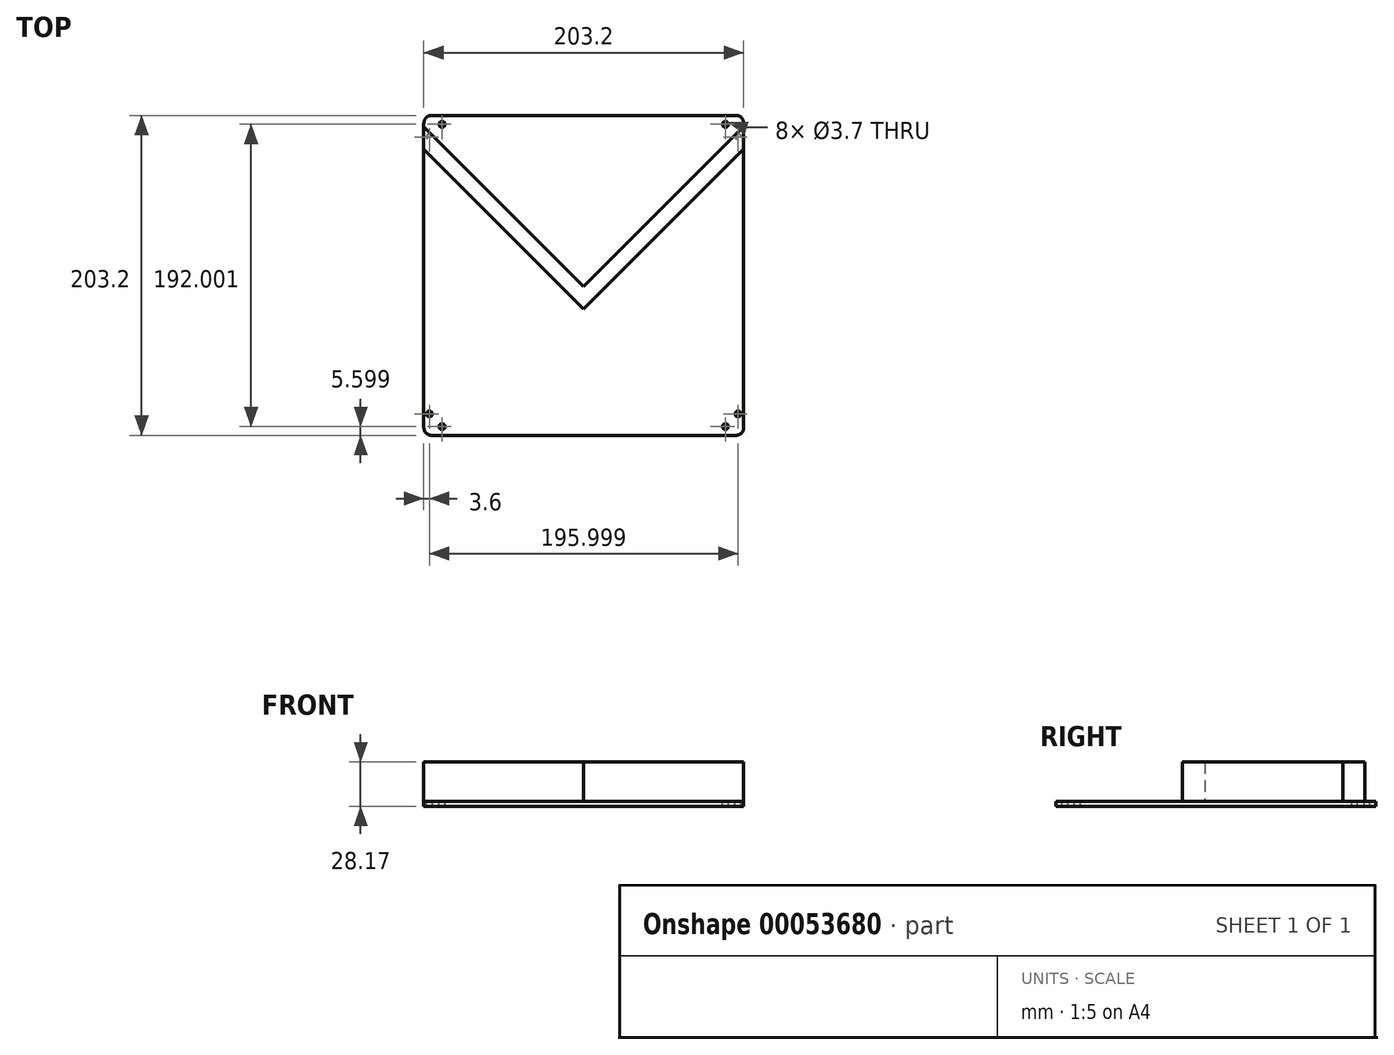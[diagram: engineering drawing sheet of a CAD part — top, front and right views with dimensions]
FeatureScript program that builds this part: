
annotation { "Feature Type Name" : "Feature", "Feature Type Description" : "" }
export const myFeature = defineFeature(function(context is Context, id is Id, definition is map)
    precondition{}
    {
        {
            var Q0;
            Q0=qCreatedBy(makeId("Top.planeOp"),FACE);
            var sketch = newSketch(context, id + "F0", { "sketchPlane" : qUnion([Q0])});
            skLineSegment(sketch, "E0.rect.bottom", {"start": v(101.6, 101.6) * mm, "end": v(-101.6, 101.6) * mm});
            skLineSegment(sketch, "E0.rect.top", {"start": v(101.6, -101.6) * mm, "end": v(-101.6, -101.6) * mm});
            skLineSegment(sketch, "E0.rect.left", {"start": v(101.6, 101.6) * mm, "end": v(101.6, -101.6) * mm});
            skLineSegment(sketch, "E0.rect.right", {"start": v(-101.6, 101.6) * mm, "end": v(-101.6, -101.6) * mm});
            skPoint(sketch, "E0.rect.middle", {"position": v(0, 0) * mm});
            skSolve(sketch);
        }
        {
            var Q0;
            Q0=makeQuery(id+"F0.imprint","IMPRINT",FACE,{"disambiguationData":[TD([[makeQuery(id+"F0.imprint","IMPRINT",EDGE,{"derivedFrom":sQuery(id+"F0.wireOp",EDGE,"E0.rect.bottom")}),1.0]])]});
            extrude(context, id + "F1", {"entities" : qUnion([Q0]), "depth" : 3.17 * mm});
        }
        {
            var Q0;
            Q0=makeQuery(id+"F1.opExtrude","CAP_FACE",FACE,{"disambiguationData":[OSD([sQuery(id+"F0.wireOp",EDGE,"E0.rect.bottom"),sQuery(id+"F0.wireOp",EDGE,"E0.rect.top"),sQuery(id+"F0.wireOp",EDGE,"E0.rect.left"),sQuery(id+"F0.wireOp",EDGE,"E0.rect.right")])],"isStart":false});
            var sketch = newSketch(context, id + "F2", { "sketchPlane" : qUnion([Q0])});
            skLineSegment(sketch, "E1", {"start": v(0, 0) * mm, "end": v(98, 0) * mm});
            skLineSegment(sketch, "E2", {"start": v(0, 0) * mm, "end": v(-98, 0) * mm});
            skLineSegment(sketch, "E3", {"start": v(98, 0) * mm, "end": v(98, 92) * mm});
            skLineSegment(sketch, "E4", {"start": v(-98, 0) * mm, "end": v(-98, 92) * mm});
            skLineSegment(sketch, "E5", {"start": v(-98, 0) * mm, "end": v(-98, -92) * mm});
            skLineSegment(sketch, "E6", {"start": v(98, 0) * mm, "end": v(98, -92) * mm});
            skArc(sketch, "E7", {"start": v(-99.85, 99.54) * mm, "mid": v(-97.04, 92.12) * mm, "end": v(-98, 100) * mm});
            skPoint(sketch, "E7.centerSnap0", {"position": v(-94, 96) * mm});
            skPoint(sketch, "E7.centerSnap1", {"position": v(-98, 100) * mm});
            skPoint(sketch, "E8", {"position": v(-98, 92) * mm});
            skArc(sketch, "E9", {"start": v(96.25, 99.6) * mm, "mid": v(98.9, 92.1) * mm, "end": v(98, 100) * mm});
            skPoint(sketch, "E9.centerSnap0", {"position": v(102, 96) * mm});
            skPoint(sketch, "E9.centerSnap1", {"position": v(98, 100) * mm});
            skPoint(sketch, "E10", {"position": v(98, 92) * mm});
            skPoint(sketch, "E11", {"position": v(98, -100) * mm});
            skPoint(sketch, "E12.centerSnap0", {"position": v(102, -96) * mm});
            skPoint(sketch, "E12.centerSnap1", {"position": v(98, -92) * mm});
            skArc(sketch, "E12", {"start": v(101.9, -95.08) * mm, "mid": v(94.03, -96.47) * mm, "end": v(102, -96) * mm});
            skPoint(sketch, "E13", {"position": v(-98, -100) * mm});
            skPoint(sketch, "E14.centerSnap0", {"position": v(-94, -96) * mm});
            skPoint(sketch, "E14.centerSnap1", {"position": v(-98, -92) * mm});
            skArc(sketch, "E14", {"start": v(-101.6, -94.26) * mm, "mid": v(-95.01, -98.66) * mm, "end": v(-100.15, -92.63) * mm});
            skPoint(sketch, "E15.right.end.orphan", {"position": v(-102, -92) * mm});
            skPoint(sketch, "E16.orphan", {"position": v(-94, -92) * mm});
            skPoint(sketch, "E17.orphan", {"position": v(-94, -100) * mm});
            skPoint(sketch, "E15.bottom.end.orphan", {"position": v(-102, -100) * mm});
            skPoint(sketch, "E18.orphan", {"position": v(-94, 100) * mm});
            skPoint(sketch, "E19.orphan", {"position": v(-94, 92) * mm});
            skPoint(sketch, "E20.orphan", {"position": v(-102, 92) * mm});
            skPoint(sketch, "E21.top.end.orphan", {"position": v(-102, 100) * mm});
            skPoint(sketch, "E22.orphan", {"position": v(102, 100) * mm});
            skPoint(sketch, "E23.orphan", {"position": v(102, 92) * mm});
            skPoint(sketch, "E24.orphan", {"position": v(94, 92) * mm});
            skPoint(sketch, "E25.right.end.orphan", {"position": v(94, 100) * mm});
            skPoint(sketch, "E26.orphan", {"position": v(102, -92) * mm});
            skPoint(sketch, "E27.orphan", {"position": v(94, -100) * mm});
            skPoint(sketch, "E28.right.end.orphan", {"position": v(94, -92) * mm});
            skPoint(sketch, "E28.bottom.start.orphan", {"position": v(102, -100) * mm});
            skCircle(sketch, "E29", {"center": v(-90, 96) * mm, "radius": 1.85 * mm});
            skCircle(sketch, "E30", {"center": v(-98, 88) * mm, "radius": 1.85 * mm});
            skCircle(sketch, "E31", {"center": v(98, 88) * mm, "radius": 1.85 * mm});
            skCircle(sketch, "E32", {"center": v(90, 96) * mm, "radius": 1.85 * mm});
            skCircle(sketch, "E33", {"center": v(98, -88) * mm, "radius": 1.85 * mm});
            skCircle(sketch, "E34", {"center": v(90, -96) * mm, "radius": 1.85 * mm});
            skCircle(sketch, "E35", {"center": v(-90, -96) * mm, "radius": 1.85 * mm});
            skCircle(sketch, "E36", {"center": v(-98, -88) * mm, "radius": 1.85 * mm});
            skPoint(sketch, "E37", {"position": v(-100.15, -92.63) * mm});
            skPoint(sketch, "E38", {"position": v(-101.6, -94.26) * mm});
            skPoint(sketch, "E39", {"position": v(-99.85, 99.54) * mm});
            skPoint(sketch, "E40", {"position": v(96.25, 99.6) * mm});
            skPoint(sketch, "E41", {"position": v(101.9, -95.08) * mm});
            skSolve(sketch);
        }
        {
            var Q0;
            Q0 = qSketchRegion(id + "F2", true);
            extrude(context, id + "F3", {"entities" : qUnion([Q0]), "operationType" : NewBodyOperationType.REMOVE, "oppositeDirection" : true, "depth" : 25.4 * mm});
        }
        {
            var Q0;
            Q0=makeQuery(id+"F1.opExtrude","SWEPT_EDGE",EDGE,{"disambiguationData":[OSD([sQuery(id+"F0.wireOp",EDGE,"E0.rect.bottom"),sQuery(id+"F0.wireOp",EDGE,"E0.rect.right")])]});
            fillet(context, id + "F4", {"entities" : qUnion([Q0]), "radius" : 5.08 * mm, "tangentPropagation" : true, "allowEdgeOverflow" : false});
        }
        {
            var Q0;
            Q0=makeQuery(id+"F1.opExtrude","SWEPT_EDGE",EDGE,{"disambiguationData":[OSD([sQuery(id+"F0.wireOp",EDGE,"E0.rect.bottom"),sQuery(id+"F0.wireOp",EDGE,"E0.rect.left")])]});
            var Q1;
            Q1=makeQuery(id+"F1.opExtrude","SWEPT_EDGE",EDGE,{"disambiguationData":[OSD([sQuery(id+"F0.wireOp",EDGE,"E0.rect.top"),sQuery(id+"F0.wireOp",EDGE,"E0.rect.left")])]});
            var Q2;
            Q2=makeQuery(id+"F1.opExtrude","SWEPT_EDGE",EDGE,{"disambiguationData":[OSD([sQuery(id+"F0.wireOp",EDGE,"E0.rect.top"),sQuery(id+"F0.wireOp",EDGE,"E0.rect.right")])]});
            fillet(context, id + "F5", {"entities" : qUnion([Q0, Q1, Q2]), "radius" : 5.08 * mm, "tangentPropagation" : true, "allowEdgeOverflow" : false});
        }
        {
            var Q0;
            Q0=makeQuery(id+"F1.opExtrude","CAP_FACE",FACE,{"disambiguationData":[OSD([sQuery(id+"F0.wireOp",EDGE,"E0.rect.bottom"),sQuery(id+"F0.wireOp",EDGE,"E0.rect.top"),sQuery(id+"F0.wireOp",EDGE,"E0.rect.left"),sQuery(id+"F0.wireOp",EDGE,"E0.rect.right")])],"isStart":false});
            var sketch = newSketch(context, id + "F6", { "sketchPlane" : qUnion([Q0])});
            skPoint(sketch, "E42", {"position": v(2.96, -10.03) * mm});
            skPoint(sketch, "E43", {"position": v(-101.6, 94.53) * mm});
            skPoint(sketch, "E44", {"position": v(101.6, 94.53) * mm});
            skPoint(sketch, "E45", {"position": v(52.93, 31.72) * mm});
            skLineSegment(sketch, "E46", {"start": v(-101.6, 94.53) * mm, "end": v(0, -7.07) * mm});
            skLineSegment(sketch, "E47", {"start": v(0, -7.07) * mm, "end": v(101.6, 94.53) * mm});
            skLineSegment(sketch, "E48", {"start": v(52.93, 31.72) * mm, "end": v(101.6, 80.39) * mm});
            skLineSegment(sketch, "E49", {"start": v(52.93, 31.72) * mm, "end": v(7.07, -14.14) * mm});
            skLineSegment(sketch, "E50", {"start": v(0, -7.07) * mm, "end": v(0, -3.45) * mm});
            skLineSegment(sketch, "E51", {"start": v(-101.6, 80.39) * mm, "end": v(-101.6, 94.53) * mm});
            skPoint(sketch, "E52", {"position": v(0, -21.21) * mm});
            skLineSegment(sketch, "E53", {"start": v(0, -21.21) * mm, "end": v(-101.6, 80.39) * mm});
            skLineSegment(sketch, "E54", {"start": v(101.6, 94.53) * mm, "end": v(101.6, 80.39) * mm});
            skPoint(sketch, "E55", {"position": v(3.89, -10.96) * mm});
            skLineSegment(sketch, "E56", {"start": v(0, -21.21) * mm, "end": v(7.07, -14.14) * mm});
            skLineSegment(sketch, "E57", {"start": v(0, -7.07) * mm, "end": v(2.96, -10.03) * mm});
            skLineSegment(sketch, "E58.trimOffspring", {"start": v(3.89, -10.96) * mm, "end": v(7.07, -14.14) * mm});
            skPoint(sketch, "E59", {"position": v(0, 0) * mm});
            skSolve(sketch);
        }
        {
            var Q0;
            Q0 = qSketchRegion(id + "F6", true);
            extrude(context, id + "F7", {"entities" : qUnion([Q0]), "depth" : 25 * mm});
        }
    });
